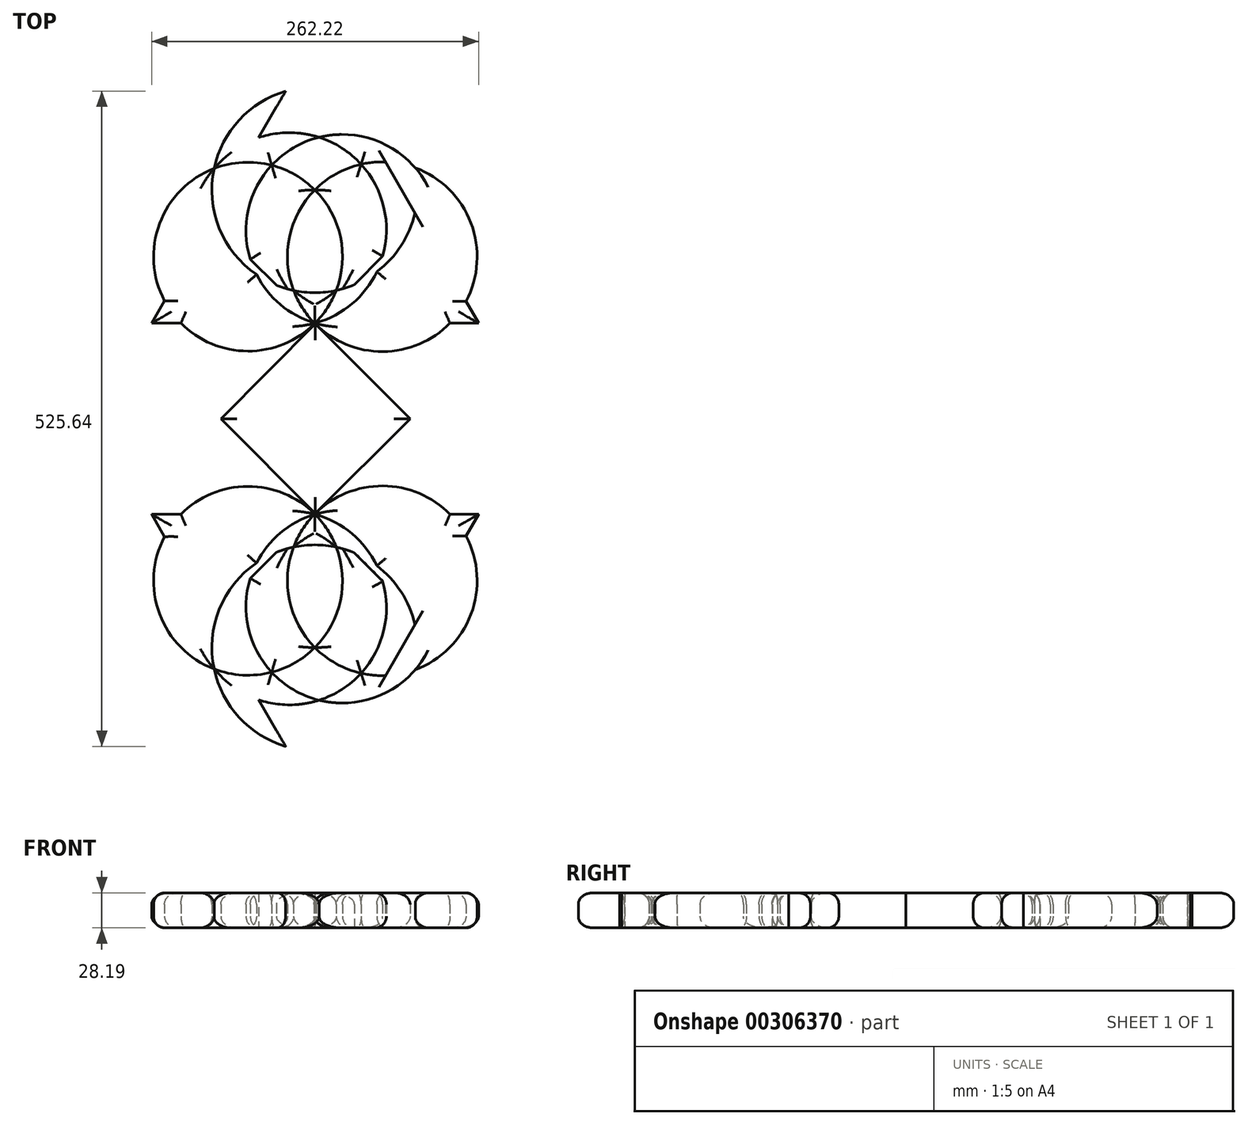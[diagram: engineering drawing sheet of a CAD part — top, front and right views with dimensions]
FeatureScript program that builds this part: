
annotation { "Feature Type Name" : "Feature", "Feature Type Description" : "" }
export const myFeature = defineFeature(function(context is Context, id is Id, definition is map)
    precondition{}
    {
        {
            var Q0;
            Q0=qCreatedBy(makeId("Top.planeOp"),FACE);
            var sketch = newSketch(context, id + "F0", { "sketchPlane" : qUnion([Q0])});
            skLineSegment(sketch, "E0", {"start": v(76.23, -76.68) * mm, "end": v(-75.62, -76.68) * mm});
            skLineSegment(sketch, "E1", {"start": v(-75.62, -76.68) * mm, "end": v(75.93, 75.47) * mm});
            skCircle(sketch, "E2", {"center": v(-53.8, 53.35) * mm, "radius": 75.78 * mm});
            skCircle(sketch, "E3", {"center": v(53.85, 53.3) * mm, "radius": 76.1 * mm});
            skCircle(sketch, "E4", {"center": v(-0.3, 107.01) * mm, "radius": 82.5 * mm});
            skLineSegment(sketch, "E5", {"start": v(76.23, -76.68) * mm, "end": v(-76.75, 76) * mm});
            skArc(sketch, "E6", {"start": v(0, 0) * mm, "mid": v(44.55, 117.58) * mm, "end": v(-81.01, 124.08) * mm});
            skArc(sketch, "E7", {"start": v(80.28, 124.67) * mm, "mid": v(-43.14, 115.96) * mm, "end": v(0, 0) * mm});
            skCircle(sketch, "E8.cCircle", {"center": v(0, 75.7) * mm, "radius": 75.7 * mm, "construction": true});
            skLineSegment(sketch, "E8.0", {"start": v(131.11, 0) * mm, "end": v(-131.11, 0) * mm});
            skLineSegment(sketch, "E8.1", {"start": v(-131.11, 0) * mm, "end": v(0, 227.1) * mm});
            skLineSegment(sketch, "E8.2", {"start": v(0, 227.1) * mm, "end": v(131.11, 0) * mm});
            skPoint(sketch, "E8.0.midPoint", {"position": v(0, 0) * mm});
            skSolve(sketch);
        }
        {
            var Q0;
            {var subQ0=sQuery(id+"F0.wireOp",EDGE,"E8.1");var subQ1=sQuery(id+"F0.wireOp",EDGE,"E2");var subQ2=makeQuery(id+"F0.imprint","INTERSECT",VERTEX,{"disambiguationData":[OD(0.0)],"derivedFrom":[subQ1,subQ0]});Q0=makeQuery(id+"F0.imprint","IMPRINT",FACE,{"disambiguationData":[TD([[makeQuery(id+"F0.imprint","IMPRINT",EDGE,{"disambiguationData":[TD([[subQ2,-1.0]])],"derivedFrom":subQ1}),-1.0]])]});}
            var Q1;
            {var subQ8=sQuery(id+"F0.wireOp",EDGE,"E8.1");var subQ9=sQuery(id+"F0.wireOp",EDGE,"E2");var subQ10=makeQuery(id+"F0.imprint","INTERSECT",VERTEX,{"disambiguationData":[OD(0.0)],"derivedFrom":[subQ9,subQ8]});Q1=makeQuery(id+"F0.imprint","IMPRINT",FACE,{"disambiguationData":[TD([[makeQuery(id+"F0.imprint","IMPRINT",EDGE,{"disambiguationData":[TD([[subQ10,-1.0]])],"derivedFrom":subQ9}),1.0]])]});}
            var Q2;
            {var subQ1=sQuery(id+"F0.wireOp",EDGE,"E4");var subQ7=sQuery(id+"F0.wireOp",EDGE,"E8.2");var subQ9=makeQuery(id+"F0.imprint","INTERSECT",VERTEX,{"disambiguationData":[OD(0.0)],"derivedFrom":[subQ1,subQ7]});Q2=makeQuery(id+"F0.imprint","IMPRINT",FACE,{"disambiguationData":[TD([[makeQuery(id+"F0.imprint","IMPRINT",EDGE,{"disambiguationData":[TD([[subQ9,-1.0]])],"derivedFrom":subQ1}),1.0]])]});}
            var Q3;
            {var subQ0=sQuery(id+"F0.wireOp",EDGE,"E8.0");var subQ1=sQuery(id+"F0.wireOp",EDGE,"E3");var subQ2=makeQuery(id+"F0.imprint","INTERSECT",VERTEX,{"disambiguationData":[OD(0.0)],"derivedFrom":[subQ1,subQ0]});Q3=makeQuery(id+"F0.imprint","IMPRINT",FACE,{"disambiguationData":[TD([[makeQuery(id+"F0.imprint","IMPRINT",EDGE,{"disambiguationData":[TD([[subQ2,-1.0]])],"derivedFrom":subQ1}),-1.0]])]});}
            var Q4;
            {var subQ1=sQuery(id+"F0.wireOp",EDGE,"E1");var subQ8=sQuery(id+"F0.wireOp",EDGE,"E8.0");var subQ12=makeQuery(id+"F0.imprint","INTERSECT",VERTEX,{"derivedFrom":[subQ1,subQ8]});Q4=makeQuery(id+"F0.imprint","IMPRINT",FACE,{"disambiguationData":[TD([[makeQuery(id+"F0.imprint","IMPRINT",EDGE,{"disambiguationData":[TD([[subQ12,-1.0]])],"derivedFrom":subQ1}),-1.0]])]});}
            var Q5;
            {var subQ0=sQuery(id+"F0.wireOp",EDGE,"E8.2");var subQ1=sQuery(id+"F0.wireOp",EDGE,"E4");var subQ2=makeQuery(id+"F0.imprint","INTERSECT",VERTEX,{"disambiguationData":[OD(0.0)],"derivedFrom":[subQ1,subQ0]});Q5=makeQuery(id+"F0.imprint","IMPRINT",FACE,{"disambiguationData":[TD([[makeQuery(id+"F0.imprint","IMPRINT",EDGE,{"disambiguationData":[TD([[subQ2,-1.0]])],"derivedFrom":subQ1}),-1.0]])]});}
            var Q6;
            {var subQ0=sQuery(id+"F0.wireOp",EDGE,"E0");Q6=makeQuery(id+"F0.imprint","IMPRINT",FACE,{"disambiguationData":[TD([[makeQuery(id+"F0.imprint","IMPRINT",EDGE,{"derivedFrom":subQ0}),-1.0]])]});}
            var Q7;
            {var subQ5=sQuery(id+"F0.wireOp",EDGE,"E2");var subQ7=sQuery(id+"F0.wireOp",EDGE,"E7");var subQ9=makeQuery(id+"F0.imprint","INTERSECT",VERTEX,{"derivedFrom":[subQ5,subQ7]});Q7=makeQuery(id+"F0.imprint","IMPRINT",FACE,{"disambiguationData":[TD([[makeQuery(id+"F0.imprint","IMPRINT",EDGE,{"disambiguationData":[TD([[subQ9,1.0]])],"derivedFrom":subQ5}),1.0]])]});}
            var Q8;
            {var subQ0=sQuery(id+"F0.wireOp",EDGE,"E4");var subQ1=sQuery(id+"F0.wireOp",EDGE,"E1");var subQ2=makeQuery(id+"F0.imprint","INTERSECT",VERTEX,{"disambiguationData":[OD(1.0)],"derivedFrom":[subQ1,subQ0]});Q8=makeQuery(id+"F0.imprint","IMPRINT",FACE,{"disambiguationData":[TD([[makeQuery(id+"F0.imprint","IMPRINT",EDGE,{"disambiguationData":[TD([[subQ2,-1.0]])],"derivedFrom":subQ1}),1.0]])]});}
            var Q9;
            {var subQ0=sQuery(id+"F0.wireOp",EDGE,"E8.2");var subQ1=sQuery(id+"F0.wireOp",EDGE,"E3");var subQ2=makeQuery(id+"F0.imprint","INTERSECT",VERTEX,{"disambiguationData":[OD(1.0)],"derivedFrom":[subQ1,subQ0]});Q9=makeQuery(id+"F0.imprint","IMPRINT",FACE,{"disambiguationData":[TD([[makeQuery(id+"F0.imprint","IMPRINT",EDGE,{"disambiguationData":[TD([[subQ2,-1.0]])],"derivedFrom":subQ1}),-1.0]])]});}
            var Q10;
            {var subQ0=sQuery(id+"F0.wireOp",EDGE,"E7");var subQ1=sQuery(id+"F0.wireOp",EDGE,"E2");var subQ2=makeQuery(id+"F0.imprint","INTERSECT",VERTEX,{"derivedFrom":[subQ1,subQ0]});Q10=makeQuery(id+"F0.imprint","IMPRINT",FACE,{"disambiguationData":[TD([[makeQuery(id+"F0.imprint","IMPRINT",EDGE,{"disambiguationData":[TD([[subQ2,-1.0]])],"derivedFrom":subQ1}),-1.0]])]});}
            var Q11;
            {var subQ3=sQuery(id+"F0.wireOp",EDGE,"E4");var subQ5=sQuery(id+"F0.wireOp",EDGE,"E3");var subQ6=makeQuery(id+"F0.imprint","INTERSECT",VERTEX,{"derivedFrom":[subQ5,subQ3]});Q11=makeQuery(id+"F0.imprint","IMPRINT",FACE,{"disambiguationData":[TD([[makeQuery(id+"F0.imprint","IMPRINT",EDGE,{"disambiguationData":[TD([[subQ6,-1.0]])],"derivedFrom":subQ5}),1.0]])]});}
            var Q12;
            {var subQ1=sQuery(id+"F0.wireOp",EDGE,"E2");var subQ3=sQuery(id+"F0.wireOp",EDGE,"E8.1");var subQ4=makeQuery(id+"F0.imprint","INTERSECT",VERTEX,{"disambiguationData":[OD(0.0)],"derivedFrom":[subQ1,subQ3]});Q12=makeQuery(id+"F0.imprint","IMPRINT",FACE,{"disambiguationData":[TD([[makeQuery(id+"F0.imprint","IMPRINT",EDGE,{"disambiguationData":[TD([[subQ4,-1.0]])],"derivedFrom":subQ3}),1.0]])]});}
            var Q13;
            {var subQ0=sQuery(id+"F0.wireOp",EDGE,"E8.0");var subQ1=sQuery(id+"F0.wireOp",EDGE,"E2");var subQ2=makeQuery(id+"F0.imprint","INTERSECT",VERTEX,{"derivedFrom":[subQ1,subQ0]});Q13=makeQuery(id+"F0.imprint","IMPRINT",FACE,{"disambiguationData":[TD([[makeQuery(id+"F0.imprint","IMPRINT",EDGE,{"disambiguationData":[TD([[subQ2,-1.0]])],"derivedFrom":subQ1}),1.0]])]});}
            var Q14;
            {var subQ0=sQuery(id+"F0.wireOp",EDGE,"E3");var subQ1=sQuery(id+"F0.wireOp",EDGE,"E1");var subQ2=makeQuery(id+"F0.imprint","INTERSECT",VERTEX,{"derivedFrom":[subQ1,subQ0]});Q14=makeQuery(id+"F0.imprint","IMPRINT",FACE,{"disambiguationData":[TD([[makeQuery(id+"F0.imprint","IMPRINT",EDGE,{"disambiguationData":[TD([[subQ2,-1.0]])],"derivedFrom":subQ1}),-1.0]])]});}
            var Q15;
            {var subQ1=sQuery(id+"F0.wireOp",EDGE,"E3");var subQ3=sQuery(id+"F0.wireOp",EDGE,"E8.2");var subQ4=makeQuery(id+"F0.imprint","INTERSECT",VERTEX,{"disambiguationData":[OD(0.0)],"derivedFrom":[subQ1,subQ3]});Q15=makeQuery(id+"F0.imprint","IMPRINT",FACE,{"disambiguationData":[TD([[makeQuery(id+"F0.imprint","IMPRINT",EDGE,{"disambiguationData":[TD([[subQ4,1.0]])],"derivedFrom":subQ3}),1.0]])]});}
            var Q16;
            {var subQ1=sQuery(id+"F0.wireOp",EDGE,"E4");var subQ3=sQuery(id+"F0.wireOp",EDGE,"E8.2");var subQ4=makeQuery(id+"F0.imprint","INTERSECT",VERTEX,{"disambiguationData":[OD(0.0)],"derivedFrom":[subQ1,subQ3]});Q16=makeQuery(id+"F0.imprint","IMPRINT",FACE,{"disambiguationData":[TD([[makeQuery(id+"F0.imprint","IMPRINT",EDGE,{"disambiguationData":[TD([[subQ4,-1.0]])],"derivedFrom":subQ3}),1.0]])]});}
            var Q17;
            {var subQ1=sQuery(id+"F0.wireOp",EDGE,"E4");var subQ3=sQuery(id+"F0.wireOp",EDGE,"E8.1");var subQ4=makeQuery(id+"F0.imprint","INTERSECT",VERTEX,{"disambiguationData":[OD(0.0)],"derivedFrom":[subQ1,subQ3]});Q17=makeQuery(id+"F0.imprint","IMPRINT",FACE,{"disambiguationData":[TD([[makeQuery(id+"F0.imprint","IMPRINT",EDGE,{"disambiguationData":[TD([[subQ4,1.0]])],"derivedFrom":subQ3}),1.0]])]});}
            var Q18;
            {var subQ1=sQuery(id+"F0.wireOp",EDGE,"E2");var subQ3=sQuery(id+"F0.wireOp",EDGE,"E8.1");var subQ4=makeQuery(id+"F0.imprint","INTERSECT",VERTEX,{"disambiguationData":[OD(1.0)],"derivedFrom":[subQ1,subQ3]});Q18=makeQuery(id+"F0.imprint","IMPRINT",FACE,{"disambiguationData":[TD([[makeQuery(id+"F0.imprint","IMPRINT",EDGE,{"disambiguationData":[TD([[subQ4,-1.0]])],"derivedFrom":subQ3}),1.0]])]});}
            var Q19;
            {var subQ1=sQuery(id+"F0.wireOp",EDGE,"E3");var subQ3=sQuery(id+"F0.wireOp",EDGE,"E8.2");var subQ4=makeQuery(id+"F0.imprint","INTERSECT",VERTEX,{"disambiguationData":[OD(1.0)],"derivedFrom":[subQ1,subQ3]});Q19=makeQuery(id+"F0.imprint","IMPRINT",FACE,{"disambiguationData":[TD([[makeQuery(id+"F0.imprint","IMPRINT",EDGE,{"disambiguationData":[TD([[subQ4,1.0]])],"derivedFrom":subQ3}),1.0]])]});}
            extrude(context, id + "F1", {"entities" : qUnion([Q0, Q1, Q2, Q3, Q4, Q5, Q6, Q7, Q8, Q9, Q10, Q11, Q12, Q13, Q14, Q15, Q16, Q17, Q18, Q19]), "depth" : 28.2 * mm});
        }
        {
            var Q0;
            {var subQ0=sQuery(id+"F0.wireOp",EDGE,"E2");Q0=makeQuery(id+"F1.opExtrude","CAP_EDGE",EDGE,{"disambiguationData":[OSD([subQ0]),TDD([makeQuery(id+"F0.imprint","IMPRINT",EDGE,{"disambiguationData":[TD([[makeQuery(id+"F0.imprint","INTERSECT",VERTEX,{"disambiguationData":[OD(0.0)],"derivedFrom":[subQ0,sQuery(id+"F0.wireOp",EDGE,"E8.1")]}),1.0]])],"derivedFrom":subQ0})])],"isStart":true});}
            var Q1;
            {var subQ0=sQuery(id+"F0.wireOp",EDGE,"E8.1");Q1=makeQuery(id+"F1.opExtrude","CAP_EDGE",EDGE,{"disambiguationData":[OSD([subQ0]),TDD([makeQuery(id+"F0.imprint","IMPRINT",EDGE,{"disambiguationData":[TD([[makeQuery(id+"F0.imprint","INTERSECT",VERTEX,{"derivedFrom":[sQuery(id+"F0.wireOp",EDGE,"E8.0"),subQ0]}),-1.0]])],"derivedFrom":subQ0})])],"isStart":true});}
            var Q2;
            {var subQ0=sQuery(id+"F0.wireOp",EDGE,"E2");Q2=makeQuery(id+"F1.opExtrude","CAP_EDGE",EDGE,{"disambiguationData":[OSD([subQ0]),TDD([makeQuery(id+"F0.imprint","IMPRINT",EDGE,{"disambiguationData":[TD([[makeQuery(id+"F0.imprint","INTERSECT",VERTEX,{"derivedFrom":[subQ0,sQuery(id+"F0.wireOp",EDGE,"E8.0")]}),-1.0]])],"derivedFrom":subQ0})])],"isStart":true});}
            var Q3;
            {var subQ0=sQuery(id+"F0.wireOp",EDGE,"E8.0");Q3=makeQuery(id+"F1.opExtrude","CAP_EDGE",EDGE,{"disambiguationData":[OSD([subQ0]),TDD([makeQuery(id+"F0.imprint","IMPRINT",EDGE,{"disambiguationData":[TD([[makeQuery(id+"F0.imprint","INTERSECT",VERTEX,{"derivedFrom":[subQ0,sQuery(id+"F0.wireOp",EDGE,"E8.1")]}),1.0]])],"derivedFrom":subQ0})])],"isStart":true});}
            var Q4;
            {var subQ0=sQuery(id+"F0.wireOp",EDGE,"E2");Q4=makeQuery(id+"F1.opExtrude","CAP_EDGE",EDGE,{"disambiguationData":[OSD([subQ0]),TDD([makeQuery(id+"F0.imprint","IMPRINT",EDGE,{"disambiguationData":[TD([[makeQuery(id+"F0.imprint","INTERSECT",VERTEX,{"derivedFrom":[subQ0,sQuery(id+"F0.wireOp",EDGE,"E8.0")]}),-1.0]])],"derivedFrom":subQ0})])],"isStart":false});}
            var Q5;
            {var subQ0=sQuery(id+"F0.wireOp",EDGE,"E8.0");Q5=makeQuery(id+"F1.opExtrude","CAP_EDGE",EDGE,{"disambiguationData":[OSD([subQ0]),TDD([makeQuery(id+"F0.imprint","IMPRINT",EDGE,{"disambiguationData":[TD([[makeQuery(id+"F0.imprint","INTERSECT",VERTEX,{"derivedFrom":[subQ0,sQuery(id+"F0.wireOp",EDGE,"E8.1")]}),1.0]])],"derivedFrom":subQ0})])],"isStart":false});}
            var Q6;
            {var subQ0=sQuery(id+"F0.wireOp",EDGE,"E2");Q6=makeQuery(id+"F1.opExtrude","CAP_EDGE",EDGE,{"disambiguationData":[OSD([subQ0]),TDD([makeQuery(id+"F0.imprint","IMPRINT",EDGE,{"disambiguationData":[TD([[makeQuery(id+"F0.imprint","INTERSECT",VERTEX,{"disambiguationData":[OD(0.0)],"derivedFrom":[subQ0,sQuery(id+"F0.wireOp",EDGE,"E8.1")]}),1.0]])],"derivedFrom":subQ0})])],"isStart":false});}
            var Q7;
            {var subQ0=sQuery(id+"F0.wireOp",EDGE,"E8.1");Q7=makeQuery(id+"F1.opExtrude","CAP_EDGE",EDGE,{"disambiguationData":[OSD([subQ0]),TDD([makeQuery(id+"F0.imprint","IMPRINT",EDGE,{"disambiguationData":[TD([[makeQuery(id+"F0.imprint","INTERSECT",VERTEX,{"derivedFrom":[sQuery(id+"F0.wireOp",EDGE,"E8.0"),subQ0]}),-1.0]])],"derivedFrom":subQ0})])],"isStart":false});}
            var Q8;
            {var subQ0=sQuery(id+"F0.wireOp",EDGE,"E4");var subQ1=makeQuery(id+"F0.imprint","INTERSECT",VERTEX,{"disambiguationData":[OD(0.0)],"derivedFrom":[subQ0,sQuery(id+"F0.wireOp",EDGE,"E5")]});var subQ2=makeQuery(id+"F0.imprint","INTERSECT",VERTEX,{"disambiguationData":[OD(1.0)],"derivedFrom":[subQ0,sQuery(id+"F0.wireOp",EDGE,"E8.1")]});Q8=makeQuery(id+"F1.opExtrude","CAP_EDGE",EDGE,{"disambiguationData":[OSD([subQ0]),TDD([makeQuery(id+"F0.imprint","IMPRINT",EDGE,{"disambiguationData":[TD([[subQ2,1.0]])],"derivedFrom":subQ0}),makeQuery(id+"F0.imprint","IMPRINT",EDGE,{"disambiguationData":[TD([[subQ1,1.0]])],"derivedFrom":subQ0}),makeQuery(id+"F0.imprint","IMPRINT",EDGE,{"disambiguationData":[TD([[subQ1,-1.0]])],"derivedFrom":subQ0})])],"isStart":true});}
            var Q9;
            {var subQ0=sQuery(id+"F0.wireOp",EDGE,"E4");Q9=makeQuery(id+"F1.opExtrude","CAP_EDGE",EDGE,{"disambiguationData":[OSD([subQ0]),TDD([makeQuery(id+"F0.imprint","IMPRINT",EDGE,{"disambiguationData":[TD([[makeQuery(id+"F0.imprint","INTERSECT",VERTEX,{"derivedFrom":[sQuery(id+"F0.wireOp",EDGE,"E3"),subQ0]}),1.0]])],"derivedFrom":subQ0})])],"isStart":true});}
            var Q10;
            {var subQ0=sQuery(id+"F0.wireOp",EDGE,"E7");Q10=makeQuery(id+"F1.opExtrude","CAP_EDGE",EDGE,{"disambiguationData":[OSD([subQ0]),TDD([makeQuery(id+"F0.imprint","IMPRINT",EDGE,{"disambiguationData":[TD([[makeQuery(id+"F0.imprint","INTERSECT",VERTEX,{"derivedFrom":[sQuery(id+"F0.wireOp",EDGE,"E4"),subQ0]}),-1.0]])],"derivedFrom":subQ0})])],"isStart":false});}
            var Q11;
            {var subQ0=sQuery(id+"F0.wireOp",EDGE,"E7");Q11=makeQuery(id+"F1.opExtrude","CAP_EDGE",EDGE,{"disambiguationData":[OSD([subQ0]),TDD([makeQuery(id+"F0.imprint","IMPRINT",EDGE,{"disambiguationData":[TD([[makeQuery(id+"F0.imprint","INTERSECT",VERTEX,{"derivedFrom":[sQuery(id+"F0.wireOp",EDGE,"E4"),subQ0]}),-1.0]])],"derivedFrom":subQ0})])],"isStart":true});}
            var Q12;
            {var subQ0=sQuery(id+"F0.wireOp",EDGE,"E4");var subQ1=makeQuery(id+"F0.imprint","INTERSECT",VERTEX,{"disambiguationData":[OD(0.0)],"derivedFrom":[subQ0,sQuery(id+"F0.wireOp",EDGE,"E5")]});var subQ2=makeQuery(id+"F0.imprint","INTERSECT",VERTEX,{"disambiguationData":[OD(1.0)],"derivedFrom":[subQ0,sQuery(id+"F0.wireOp",EDGE,"E8.1")]});Q12=makeQuery(id+"F1.opExtrude","CAP_EDGE",EDGE,{"disambiguationData":[OSD([subQ0]),TDD([makeQuery(id+"F0.imprint","IMPRINT",EDGE,{"disambiguationData":[TD([[subQ2,1.0]])],"derivedFrom":subQ0}),makeQuery(id+"F0.imprint","IMPRINT",EDGE,{"disambiguationData":[TD([[subQ1,1.0]])],"derivedFrom":subQ0}),makeQuery(id+"F0.imprint","IMPRINT",EDGE,{"disambiguationData":[TD([[subQ1,-1.0]])],"derivedFrom":subQ0})])],"isStart":false});}
            var Q13;
            {var subQ0=sQuery(id+"F0.wireOp",EDGE,"E5");Q13=makeQuery(id+"F1.opExtrude","CAP_EDGE",EDGE,{"disambiguationData":[OSD([subQ0]),TDD([makeQuery(id+"F0.imprint","IMPRINT",EDGE,{"disambiguationData":[TD([[makeQuery(id+"F0.imprint","INTERSECT",VERTEX,{"disambiguationData":[OD(1.0)],"derivedFrom":[sQuery(id+"F0.wireOp",EDGE,"E4"),subQ0]}),-1.0]])],"derivedFrom":subQ0})])],"isStart":false});}
            var Q14;
            {var subQ0=sQuery(id+"F0.wireOp",EDGE,"E4");Q14=makeQuery(id+"F1.opExtrude","CAP_EDGE",EDGE,{"disambiguationData":[OSD([subQ0]),TDD([makeQuery(id+"F0.imprint","IMPRINT",EDGE,{"disambiguationData":[TD([[makeQuery(id+"F0.imprint","INTERSECT",VERTEX,{"derivedFrom":[sQuery(id+"F0.wireOp",EDGE,"E3"),subQ0]}),1.0]])],"derivedFrom":subQ0})])],"isStart":false});}
            var Q15;
            {var subQ0=sQuery(id+"F0.wireOp",EDGE,"E5");Q15=makeQuery(id+"F1.opExtrude","CAP_EDGE",EDGE,{"disambiguationData":[OSD([subQ0]),TDD([makeQuery(id+"F0.imprint","IMPRINT",EDGE,{"disambiguationData":[TD([[makeQuery(id+"F0.imprint","INTERSECT",VERTEX,{"disambiguationData":[OD(1.0)],"derivedFrom":[sQuery(id+"F0.wireOp",EDGE,"E4"),subQ0]}),-1.0]])],"derivedFrom":subQ0})])],"isStart":true});}
            var Q16;
            {var subQ0=sQuery(id+"F0.wireOp",EDGE,"E7");Q16=makeQuery(id+"F1.opExtrude","CAP_EDGE",EDGE,{"disambiguationData":[OSD([subQ0]),TDD([makeQuery(id+"F0.imprint","IMPRINT",EDGE,{"disambiguationData":[TD([[makeQuery(id+"F0.imprint","INTERSECT",VERTEX,{"derivedFrom":[sQuery(id+"F0.wireOp",EDGE,"E2"),subQ0]}),-1.0]])],"derivedFrom":subQ0})])],"isStart":false});}
            var Q17;
            {var subQ0=sQuery(id+"F0.wireOp",EDGE,"E7");Q17=makeQuery(id+"F1.opExtrude","CAP_EDGE",EDGE,{"disambiguationData":[OSD([subQ0]),TDD([makeQuery(id+"F0.imprint","IMPRINT",EDGE,{"disambiguationData":[TD([[makeQuery(id+"F0.imprint","INTERSECT",VERTEX,{"derivedFrom":[sQuery(id+"F0.wireOp",EDGE,"E2"),subQ0]}),-1.0]])],"derivedFrom":subQ0})])],"isStart":true});}
            var Q18;
            {var subQ0=sQuery(id+"F0.wireOp",EDGE,"E2");Q18=makeQuery(id+"F1.opExtrude","CAP_EDGE",EDGE,{"disambiguationData":[OSD([subQ0]),TDD([makeQuery(id+"F0.imprint","IMPRINT",EDGE,{"disambiguationData":[TD([[makeQuery(id+"F0.imprint","INTERSECT",VERTEX,{"derivedFrom":[subQ0,sQuery(id+"F0.wireOp",EDGE,"E7")]}),1.0]])],"derivedFrom":subQ0})])],"isStart":false});}
            var Q19;
            {var subQ0=sQuery(id+"F0.wireOp",EDGE,"E3");Q19=makeQuery(id+"F1.opExtrude","CAP_EDGE",EDGE,{"disambiguationData":[OSD([subQ0]),TDD([makeQuery(id+"F0.imprint","IMPRINT",EDGE,{"disambiguationData":[TD([[makeQuery(id+"F0.imprint","INTERSECT",VERTEX,{"disambiguationData":[OD(0.0)],"derivedFrom":[sQuery(id+"F0.wireOp",EDGE,"E2"),subQ0]}),-1.0]])],"derivedFrom":subQ0})])],"isStart":false});}
            var Q20;
            {var subQ0=sQuery(id+"F0.wireOp",EDGE,"E2");Q20=makeQuery(id+"F1.opExtrude","CAP_EDGE",EDGE,{"disambiguationData":[OSD([subQ0]),TDD([makeQuery(id+"F0.imprint","IMPRINT",EDGE,{"disambiguationData":[TD([[makeQuery(id+"F0.imprint","INTERSECT",VERTEX,{"disambiguationData":[OD(0.0)],"derivedFrom":[subQ0,sQuery(id+"F0.wireOp",EDGE,"E3")]}),1.0]])],"derivedFrom":subQ0})])],"isStart":false});}
            var Q21;
            {var subQ0=sQuery(id+"F0.wireOp",EDGE,"E2");Q21=makeQuery(id+"F1.opExtrude","CAP_EDGE",EDGE,{"disambiguationData":[OSD([subQ0]),TDD([makeQuery(id+"F0.imprint","IMPRINT",EDGE,{"disambiguationData":[TD([[makeQuery(id+"F0.imprint","INTERSECT",VERTEX,{"disambiguationData":[OD(0.0)],"derivedFrom":[subQ0,sQuery(id+"F0.wireOp",EDGE,"E3")]}),1.0]])],"derivedFrom":subQ0})])],"isStart":true});}
            var Q22;
            {var subQ0=sQuery(id+"F0.wireOp",EDGE,"E3");Q22=makeQuery(id+"F1.opExtrude","CAP_EDGE",EDGE,{"disambiguationData":[OSD([subQ0]),TDD([makeQuery(id+"F0.imprint","IMPRINT",EDGE,{"disambiguationData":[TD([[makeQuery(id+"F0.imprint","INTERSECT",VERTEX,{"disambiguationData":[OD(0.0)],"derivedFrom":[sQuery(id+"F0.wireOp",EDGE,"E2"),subQ0]}),1.0]])],"derivedFrom":subQ0})])],"isStart":false});}
            var Q23;
            {var subQ0=sQuery(id+"F0.wireOp",EDGE,"E3");Q23=makeQuery(id+"F1.opExtrude","CAP_EDGE",EDGE,{"disambiguationData":[OSD([subQ0]),TDD([makeQuery(id+"F0.imprint","IMPRINT",EDGE,{"disambiguationData":[TD([[makeQuery(id+"F0.imprint","INTERSECT",VERTEX,{"disambiguationData":[OD(0.0)],"derivedFrom":[sQuery(id+"F0.wireOp",EDGE,"E2"),subQ0]}),1.0]])],"derivedFrom":subQ0})])],"isStart":true});}
            var Q24;
            {var subQ0=sQuery(id+"F0.wireOp",EDGE,"E6");Q24=makeQuery(id+"F1.opExtrude","CAP_EDGE",EDGE,{"disambiguationData":[OSD([subQ0]),TDD([makeQuery(id+"F0.imprint","IMPRINT",EDGE,{"disambiguationData":[TD([[makeQuery(id+"F0.imprint","INTERSECT",VERTEX,{"disambiguationData":[OD(1.0)],"derivedFrom":[sQuery(id+"F0.wireOp",EDGE,"E1"),subQ0]}),-1.0]])],"derivedFrom":subQ0})])],"isStart":false});}
            var Q25;
            {var subQ0=sQuery(id+"F0.wireOp",EDGE,"E1");Q25=makeQuery(id+"F1.opExtrude","CAP_EDGE",EDGE,{"disambiguationData":[OSD([subQ0]),TDD([makeQuery(id+"F0.imprint","IMPRINT",EDGE,{"disambiguationData":[TD([[makeQuery(id+"F0.imprint","INTERSECT",VERTEX,{"disambiguationData":[OD(1.0)],"derivedFrom":[subQ0,sQuery(id+"F0.wireOp",EDGE,"E4")]}),-1.0]])],"derivedFrom":subQ0})])],"isStart":false});}
            var Q26;
            {var subQ0=sQuery(id+"F0.wireOp",EDGE,"E3");Q26=makeQuery(id+"F1.opExtrude","CAP_EDGE",EDGE,{"disambiguationData":[OSD([subQ0]),TDD([makeQuery(id+"F0.imprint","IMPRINT",EDGE,{"disambiguationData":[TD([[makeQuery(id+"F0.imprint","INTERSECT",VERTEX,{"derivedFrom":[sQuery(id+"F0.wireOp",EDGE,"E1"),subQ0]}),-1.0]])],"derivedFrom":subQ0})])],"isStart":false});}
            var Q27;
            {var subQ0=sQuery(id+"F0.wireOp",EDGE,"E8.0");Q27=makeQuery(id+"F1.opExtrude","CAP_EDGE",EDGE,{"disambiguationData":[OSD([subQ0]),TDD([makeQuery(id+"F0.imprint","IMPRINT",EDGE,{"disambiguationData":[TD([[makeQuery(id+"F0.imprint","INTERSECT",VERTEX,{"derivedFrom":[subQ0,sQuery(id+"F0.wireOp",EDGE,"E8.2")]}),-1.0]])],"derivedFrom":subQ0})])],"isStart":false});}
            var Q28;
            {var subQ0=sQuery(id+"F0.wireOp",EDGE,"E4");var subQ1=makeQuery(id+"F0.imprint","INTERSECT",VERTEX,{"disambiguationData":[OD(1.0)],"derivedFrom":[subQ0,sQuery(id+"F0.wireOp",EDGE,"E8.2")]});var subQ2=makeQuery(id+"F0.imprint","INTERSECT",VERTEX,{"disambiguationData":[OD(0.0)],"derivedFrom":[sQuery(id+"F0.wireOp",EDGE,"E1"),subQ0]});Q28=makeQuery(id+"F1.opExtrude","CAP_EDGE",EDGE,{"disambiguationData":[OSD([subQ0]),TDD([makeQuery(id+"F0.imprint","IMPRINT",EDGE,{"disambiguationData":[TD([[subQ2,1.0]])],"derivedFrom":subQ0}),makeQuery(id+"F0.imprint","IMPRINT",EDGE,{"disambiguationData":[TD([[subQ2,-1.0]])],"derivedFrom":subQ0}),makeQuery(id+"F0.imprint","IMPRINT",EDGE,{"disambiguationData":[TD([[subQ1,-1.0]])],"derivedFrom":subQ0})])],"isStart":false});}
            var Q29;
            {var subQ0=sQuery(id+"F0.wireOp",EDGE,"E6");Q29=makeQuery(id+"F1.opExtrude","CAP_EDGE",EDGE,{"disambiguationData":[OSD([subQ0]),TDD([makeQuery(id+"F0.imprint","IMPRINT",EDGE,{"disambiguationData":[TD([[makeQuery(id+"F0.imprint","INTERSECT",VERTEX,{"disambiguationData":[OD(0.0)],"derivedFrom":[sQuery(id+"F0.wireOp",EDGE,"E1"),subQ0]}),-1.0]])],"derivedFrom":subQ0})])],"isStart":false});}
            var Q30;
            {var subQ0=sQuery(id+"F0.wireOp",EDGE,"E4");Q30=makeQuery(id+"F1.opExtrude","CAP_EDGE",EDGE,{"disambiguationData":[OSD([subQ0]),TDD([makeQuery(id+"F0.imprint","IMPRINT",EDGE,{"disambiguationData":[TD([[makeQuery(id+"F0.imprint","INTERSECT",VERTEX,{"disambiguationData":[OD(1.0)],"derivedFrom":[sQuery(id+"F0.wireOp",EDGE,"E1"),subQ0]}),1.0]])],"derivedFrom":subQ0})])],"isStart":false});}
            var Q31;
            {var subQ0=sQuery(id+"F0.wireOp",EDGE,"E6");Q31=makeQuery(id+"F1.opExtrude","CAP_EDGE",EDGE,{"disambiguationData":[OSD([subQ0]),TDD([makeQuery(id+"F0.imprint","IMPRINT",EDGE,{"disambiguationData":[TD([[makeQuery(id+"F0.imprint","INTERSECT",VERTEX,{"disambiguationData":[OD(0.0)],"derivedFrom":[sQuery(id+"F0.wireOp",EDGE,"E1"),subQ0]}),-1.0]])],"derivedFrom":subQ0})])],"isStart":true});}
            var Q32;
            {var subQ0=sQuery(id+"F0.wireOp",EDGE,"E4");var subQ1=makeQuery(id+"F0.imprint","INTERSECT",VERTEX,{"disambiguationData":[OD(1.0)],"derivedFrom":[subQ0,sQuery(id+"F0.wireOp",EDGE,"E8.2")]});var subQ2=makeQuery(id+"F0.imprint","INTERSECT",VERTEX,{"disambiguationData":[OD(0.0)],"derivedFrom":[sQuery(id+"F0.wireOp",EDGE,"E1"),subQ0]});Q32=makeQuery(id+"F1.opExtrude","CAP_EDGE",EDGE,{"disambiguationData":[OSD([subQ0]),TDD([makeQuery(id+"F0.imprint","IMPRINT",EDGE,{"disambiguationData":[TD([[subQ2,1.0]])],"derivedFrom":subQ0}),makeQuery(id+"F0.imprint","IMPRINT",EDGE,{"disambiguationData":[TD([[subQ2,-1.0]])],"derivedFrom":subQ0}),makeQuery(id+"F0.imprint","IMPRINT",EDGE,{"disambiguationData":[TD([[subQ1,-1.0]])],"derivedFrom":subQ0})])],"isStart":true});}
            var Q33;
            {var subQ0=sQuery(id+"F0.wireOp",EDGE,"E6");Q33=makeQuery(id+"F1.opExtrude","CAP_EDGE",EDGE,{"disambiguationData":[OSD([subQ0]),TDD([makeQuery(id+"F0.imprint","IMPRINT",EDGE,{"disambiguationData":[TD([[makeQuery(id+"F0.imprint","INTERSECT",VERTEX,{"derivedFrom":[sQuery(id+"F0.wireOp",EDGE,"E3"),subQ0]}),-1.0]])],"derivedFrom":subQ0})])],"isStart":false});}
            var Q34;
            {var subQ0=sQuery(id+"F0.wireOp",EDGE,"E3");var subQ1=makeQuery(id+"F0.imprint","INTERSECT",VERTEX,{"disambiguationData":[OD(1.0)],"derivedFrom":[subQ0,sQuery(id+"F0.wireOp",EDGE,"E8.2")]});Q34=makeQuery(id+"F1.opExtrude","CAP_EDGE",EDGE,{"disambiguationData":[OSD([subQ0]),TDD([makeQuery(id+"F0.imprint","IMPRINT",EDGE,{"disambiguationData":[TD([[subQ1,1.0]])],"derivedFrom":subQ0}),makeQuery(id+"F0.imprint","IMPRINT",EDGE,{"disambiguationData":[TD([[subQ1,-1.0]])],"derivedFrom":subQ0})])],"isStart":false});}
            var Q35;
            {var subQ0=sQuery(id+"F0.wireOp",EDGE,"E7");Q35=makeQuery(id+"F1.opExtrude","CAP_EDGE",EDGE,{"disambiguationData":[OSD([subQ0]),TDD([makeQuery(id+"F0.imprint","IMPRINT",EDGE,{"disambiguationData":[TD([[makeQuery(id+"F0.imprint","INTERSECT",VERTEX,{"derivedFrom":[sQuery(id+"F0.wireOp",EDGE,"E2"),subQ0]}),1.0]])],"derivedFrom":subQ0})])],"isStart":false});}
            var Q36;
            {var subQ0=sQuery(id+"F0.wireOp",EDGE,"E4");Q36=makeQuery(id+"F1.opExtrude","CAP_EDGE",EDGE,{"disambiguationData":[OSD([subQ0]),TDD([makeQuery(id+"F0.imprint","IMPRINT",EDGE,{"disambiguationData":[TD([[makeQuery(id+"F0.imprint","INTERSECT",VERTEX,{"disambiguationData":[OD(0.0)],"derivedFrom":[subQ0,sQuery(id+"F0.wireOp",EDGE,"E8.1")]}),-1.0]])],"derivedFrom":subQ0})])],"isStart":false});}
            var Q37;
            {var subQ0=sQuery(id+"F0.wireOp",EDGE,"E4");Q37=makeQuery(id+"F1.opExtrude","CAP_EDGE",EDGE,{"disambiguationData":[OSD([subQ0]),TDD([makeQuery(id+"F0.imprint","IMPRINT",EDGE,{"disambiguationData":[TD([[makeQuery(id+"F0.imprint","INTERSECT",VERTEX,{"disambiguationData":[OD(0.0)],"derivedFrom":[subQ0,sQuery(id+"F0.wireOp",EDGE,"E8.1")]}),-1.0]])],"derivedFrom":subQ0})])],"isStart":true});}
            var Q38;
            {var subQ0=sQuery(id+"F0.wireOp",EDGE,"E2");var subQ1=makeQuery(id+"F0.imprint","INTERSECT",VERTEX,{"disambiguationData":[OD(1.0)],"derivedFrom":[subQ0,sQuery(id+"F0.wireOp",EDGE,"E8.1")]});Q38=makeQuery(id+"F1.opExtrude","CAP_EDGE",EDGE,{"disambiguationData":[OSD([subQ0]),TDD([makeQuery(id+"F0.imprint","IMPRINT",EDGE,{"disambiguationData":[TD([[makeQuery(id+"F0.imprint","INTERSECT",VERTEX,{"derivedFrom":[subQ0,sQuery(id+"F0.wireOp",EDGE,"E7")]}),-1.0]])],"derivedFrom":subQ0}),makeQuery(id+"F0.imprint","IMPRINT",EDGE,{"disambiguationData":[TD([[subQ1,-1.0]])],"derivedFrom":subQ0})])],"isStart":false});}
            var Q39;
            {var subQ0=sQuery(id+"F0.wireOp",EDGE,"E8.1");Q39=makeQuery(id+"F1.opExtrude","CAP_EDGE",EDGE,{"disambiguationData":[OSD([subQ0]),TDD([makeQuery(id+"F0.imprint","IMPRINT",EDGE,{"disambiguationData":[TD([[makeQuery(id+"F0.imprint","INTERSECT",VERTEX,{"derivedFrom":[subQ0,sQuery(id+"F0.wireOp",EDGE,"E8.2")]}),1.0]])],"derivedFrom":subQ0})])],"isStart":false});}
            var Q40;
            {var subQ0=sQuery(id+"F0.wireOp",EDGE,"E8.2");Q40=makeQuery(id+"F1.opExtrude","CAP_EDGE",EDGE,{"disambiguationData":[OSD([subQ0]),TDD([makeQuery(id+"F0.imprint","IMPRINT",EDGE,{"disambiguationData":[TD([[makeQuery(id+"F0.imprint","INTERSECT",VERTEX,{"derivedFrom":[sQuery(id+"F0.wireOp",EDGE,"E8.1"),subQ0]}),-1.0]])],"derivedFrom":subQ0})])],"isStart":false});}
            var Q41;
            {var subQ0=sQuery(id+"F0.wireOp",EDGE,"E4");Q41=makeQuery(id+"F1.opExtrude","CAP_EDGE",EDGE,{"disambiguationData":[OSD([subQ0]),TDD([makeQuery(id+"F0.imprint","IMPRINT",EDGE,{"disambiguationData":[TD([[makeQuery(id+"F0.imprint","INTERSECT",VERTEX,{"disambiguationData":[OD(0.0)],"derivedFrom":[subQ0,sQuery(id+"F0.wireOp",EDGE,"E8.2")]}),1.0]])],"derivedFrom":subQ0})])],"isStart":false});}
            var Q42;
            {var subQ0=sQuery(id+"F0.wireOp",EDGE,"E8.1");Q42=makeQuery(id+"F1.opExtrude","CAP_EDGE",EDGE,{"disambiguationData":[OSD([subQ0]),TDD([makeQuery(id+"F0.imprint","IMPRINT",EDGE,{"disambiguationData":[TD([[makeQuery(id+"F0.imprint","INTERSECT",VERTEX,{"derivedFrom":[subQ0,sQuery(id+"F0.wireOp",EDGE,"E8.2")]}),1.0]])],"derivedFrom":subQ0})])],"isStart":true});}
            var Q43;
            {var subQ0=sQuery(id+"F0.wireOp",EDGE,"E3");Q43=makeQuery(id+"F1.opExtrude","CAP_EDGE",EDGE,{"disambiguationData":[OSD([subQ0]),TDD([makeQuery(id+"F0.imprint","IMPRINT",EDGE,{"disambiguationData":[TD([[makeQuery(id+"F0.imprint","INTERSECT",VERTEX,{"disambiguationData":[OD(0.0)],"derivedFrom":[subQ0,sQuery(id+"F0.wireOp",EDGE,"E8.2")]}),-1.0]])],"derivedFrom":subQ0})])],"isStart":false});}
            var Q44;
            {var subQ0=sQuery(id+"F0.wireOp",EDGE,"E8.2");Q44=makeQuery(id+"F1.opExtrude","CAP_EDGE",EDGE,{"disambiguationData":[OSD([subQ0]),TDD([makeQuery(id+"F0.imprint","IMPRINT",EDGE,{"disambiguationData":[TD([[makeQuery(id+"F0.imprint","INTERSECT",VERTEX,{"derivedFrom":[sQuery(id+"F0.wireOp",EDGE,"E8.0"),subQ0]}),1.0]])],"derivedFrom":subQ0})])],"isStart":false});}
            var Q45;
            {var subQ0=sQuery(id+"F0.wireOp",EDGE,"E2");Q45=makeQuery(id+"F1.opExtrude","CAP_EDGE",EDGE,{"disambiguationData":[OSD([subQ0]),TDD([makeQuery(id+"F0.imprint","IMPRINT",EDGE,{"disambiguationData":[TD([[makeQuery(id+"F0.imprint","INTERSECT",VERTEX,{"derivedFrom":[subQ0,sQuery(id+"F0.wireOp",EDGE,"E4")]}),1.0]])],"derivedFrom":subQ0})])],"isStart":false});}
            var Q46;
            {var subQ0=sQuery(id+"F0.wireOp",EDGE,"E4");Q46=makeQuery(id+"F1.opExtrude","CAP_EDGE",EDGE,{"disambiguationData":[OSD([subQ0]),TDD([makeQuery(id+"F0.imprint","IMPRINT",EDGE,{"disambiguationData":[TD([[makeQuery(id+"F0.imprint","INTERSECT",VERTEX,{"derivedFrom":[sQuery(id+"F0.wireOp",EDGE,"E2"),subQ0]}),1.0]])],"derivedFrom":subQ0})])],"isStart":false});}
            var Q47;
            {var subQ0=sQuery(id+"F0.wireOp",EDGE,"E4");Q47=makeQuery(id+"F1.opExtrude","CAP_EDGE",EDGE,{"disambiguationData":[OSD([subQ0]),TDD([makeQuery(id+"F0.imprint","IMPRINT",EDGE,{"disambiguationData":[TD([[makeQuery(id+"F0.imprint","INTERSECT",VERTEX,{"derivedFrom":[sQuery(id+"F0.wireOp",EDGE,"E2"),subQ0]}),1.0]])],"derivedFrom":subQ0})])],"isStart":true});}
            var Q48;
            {var subQ0=sQuery(id+"F0.wireOp",EDGE,"E3");Q48=makeQuery(id+"F1.opExtrude","CAP_EDGE",EDGE,{"disambiguationData":[OSD([subQ0]),TDD([makeQuery(id+"F0.imprint","IMPRINT",EDGE,{"disambiguationData":[TD([[makeQuery(id+"F0.imprint","INTERSECT",VERTEX,{"derivedFrom":[subQ0,sQuery(id+"F0.wireOp",EDGE,"E4")]}),-1.0]])],"derivedFrom":subQ0})])],"isStart":false});}
            var Q49;
            {var subQ0=sQuery(id+"F0.wireOp",EDGE,"E3");Q49=makeQuery(id+"F1.opExtrude","CAP_EDGE",EDGE,{"disambiguationData":[OSD([subQ0]),TDD([makeQuery(id+"F0.imprint","IMPRINT",EDGE,{"disambiguationData":[TD([[makeQuery(id+"F0.imprint","INTERSECT",VERTEX,{"derivedFrom":[subQ0,sQuery(id+"F0.wireOp",EDGE,"E4")]}),-1.0]])],"derivedFrom":subQ0})])],"isStart":true});}
            var Q50;
            {var subQ0=sQuery(id+"F0.wireOp",EDGE,"E4");Q50=makeQuery(id+"F1.opExtrude","CAP_EDGE",EDGE,{"disambiguationData":[OSD([subQ0]),TDD([makeQuery(id+"F0.imprint","IMPRINT",EDGE,{"disambiguationData":[TD([[makeQuery(id+"F0.imprint","INTERSECT",VERTEX,{"disambiguationData":[OD(0.0)],"derivedFrom":[subQ0,sQuery(id+"F0.wireOp",EDGE,"E8.2")]}),1.0]])],"derivedFrom":subQ0})])],"isStart":true});}
            var Q51;
            {var subQ0=sQuery(id+"F0.wireOp",EDGE,"E8.2");Q51=makeQuery(id+"F1.opExtrude","CAP_EDGE",EDGE,{"disambiguationData":[OSD([subQ0]),TDD([makeQuery(id+"F0.imprint","IMPRINT",EDGE,{"disambiguationData":[TD([[makeQuery(id+"F0.imprint","INTERSECT",VERTEX,{"derivedFrom":[sQuery(id+"F0.wireOp",EDGE,"E8.1"),subQ0]}),-1.0]])],"derivedFrom":subQ0})])],"isStart":true});}
            var Q52;
            {var subQ0=sQuery(id+"F0.wireOp",EDGE,"E7");Q52=makeQuery(id+"F1.opExtrude","CAP_EDGE",EDGE,{"disambiguationData":[OSD([subQ0]),TDD([makeQuery(id+"F0.imprint","IMPRINT",EDGE,{"disambiguationData":[TD([[makeQuery(id+"F0.imprint","INTERSECT",VERTEX,{"derivedFrom":[sQuery(id+"F0.wireOp",EDGE,"E2"),subQ0]}),1.0]])],"derivedFrom":subQ0})])],"isStart":true});}
            var Q53;
            {var subQ0=sQuery(id+"F0.wireOp",EDGE,"E6");Q53=makeQuery(id+"F1.opExtrude","CAP_EDGE",EDGE,{"disambiguationData":[OSD([subQ0]),TDD([makeQuery(id+"F0.imprint","IMPRINT",EDGE,{"disambiguationData":[TD([[makeQuery(id+"F0.imprint","INTERSECT",VERTEX,{"derivedFrom":[sQuery(id+"F0.wireOp",EDGE,"E3"),subQ0]}),-1.0]])],"derivedFrom":subQ0})])],"isStart":true});}
            var Q54;
            {var subQ0=sQuery(id+"F0.wireOp",EDGE,"E3");var subQ1=makeQuery(id+"F0.imprint","INTERSECT",VERTEX,{"disambiguationData":[OD(1.0)],"derivedFrom":[subQ0,sQuery(id+"F0.wireOp",EDGE,"E8.2")]});Q54=makeQuery(id+"F1.opExtrude","CAP_EDGE",EDGE,{"disambiguationData":[OSD([subQ0]),TDD([makeQuery(id+"F0.imprint","IMPRINT",EDGE,{"disambiguationData":[TD([[subQ1,1.0]])],"derivedFrom":subQ0}),makeQuery(id+"F0.imprint","IMPRINT",EDGE,{"disambiguationData":[TD([[subQ1,-1.0]])],"derivedFrom":subQ0})])],"isStart":true});}
            var Q55;
            {var subQ0=sQuery(id+"F0.wireOp",EDGE,"E2");var subQ1=makeQuery(id+"F0.imprint","INTERSECT",VERTEX,{"disambiguationData":[OD(1.0)],"derivedFrom":[subQ0,sQuery(id+"F0.wireOp",EDGE,"E8.1")]});Q55=makeQuery(id+"F1.opExtrude","CAP_EDGE",EDGE,{"disambiguationData":[OSD([subQ0]),TDD([makeQuery(id+"F0.imprint","IMPRINT",EDGE,{"disambiguationData":[TD([[makeQuery(id+"F0.imprint","INTERSECT",VERTEX,{"derivedFrom":[subQ0,sQuery(id+"F0.wireOp",EDGE,"E7")]}),-1.0]])],"derivedFrom":subQ0}),makeQuery(id+"F0.imprint","IMPRINT",EDGE,{"disambiguationData":[TD([[subQ1,-1.0]])],"derivedFrom":subQ0})])],"isStart":true});}
            var Q56;
            {var subQ0=sQuery(id+"F0.wireOp",EDGE,"E2");Q56=makeQuery(id+"F1.opExtrude","CAP_EDGE",EDGE,{"disambiguationData":[OSD([subQ0]),TDD([makeQuery(id+"F0.imprint","IMPRINT",EDGE,{"disambiguationData":[TD([[makeQuery(id+"F0.imprint","INTERSECT",VERTEX,{"derivedFrom":[subQ0,sQuery(id+"F0.wireOp",EDGE,"E7")]}),1.0]])],"derivedFrom":subQ0})])],"isStart":true});}
            var Q57;
            {var subQ0=sQuery(id+"F0.wireOp",EDGE,"E3");Q57=makeQuery(id+"F1.opExtrude","CAP_EDGE",EDGE,{"disambiguationData":[OSD([subQ0]),TDD([makeQuery(id+"F0.imprint","IMPRINT",EDGE,{"disambiguationData":[TD([[makeQuery(id+"F0.imprint","INTERSECT",VERTEX,{"disambiguationData":[OD(0.0)],"derivedFrom":[sQuery(id+"F0.wireOp",EDGE,"E2"),subQ0]}),-1.0]])],"derivedFrom":subQ0})])],"isStart":true});}
            var Q58;
            {var subQ0=sQuery(id+"F0.wireOp",EDGE,"E6");Q58=makeQuery(id+"F1.opExtrude","CAP_EDGE",EDGE,{"disambiguationData":[OSD([subQ0]),TDD([makeQuery(id+"F0.imprint","IMPRINT",EDGE,{"disambiguationData":[TD([[makeQuery(id+"F0.imprint","INTERSECT",VERTEX,{"disambiguationData":[OD(1.0)],"derivedFrom":[sQuery(id+"F0.wireOp",EDGE,"E1"),subQ0]}),-1.0]])],"derivedFrom":subQ0})])],"isStart":true});}
            var Q59;
            {var subQ0=sQuery(id+"F0.wireOp",EDGE,"E3");Q59=makeQuery(id+"F1.opExtrude","CAP_EDGE",EDGE,{"disambiguationData":[OSD([subQ0]),TDD([makeQuery(id+"F0.imprint","IMPRINT",EDGE,{"disambiguationData":[TD([[makeQuery(id+"F0.imprint","INTERSECT",VERTEX,{"disambiguationData":[OD(0.0)],"derivedFrom":[subQ0,sQuery(id+"F0.wireOp",EDGE,"E8.2")]}),-1.0]])],"derivedFrom":subQ0})])],"isStart":true});}
            var Q60;
            {var subQ0=sQuery(id+"F0.wireOp",EDGE,"E8.2");Q60=makeQuery(id+"F1.opExtrude","CAP_EDGE",EDGE,{"disambiguationData":[OSD([subQ0]),TDD([makeQuery(id+"F0.imprint","IMPRINT",EDGE,{"disambiguationData":[TD([[makeQuery(id+"F0.imprint","INTERSECT",VERTEX,{"derivedFrom":[sQuery(id+"F0.wireOp",EDGE,"E8.0"),subQ0]}),1.0]])],"derivedFrom":subQ0})])],"isStart":true});}
            var Q61;
            {var subQ0=sQuery(id+"F0.wireOp",EDGE,"E8.0");Q61=makeQuery(id+"F1.opExtrude","CAP_EDGE",EDGE,{"disambiguationData":[OSD([subQ0]),TDD([makeQuery(id+"F0.imprint","IMPRINT",EDGE,{"disambiguationData":[TD([[makeQuery(id+"F0.imprint","INTERSECT",VERTEX,{"derivedFrom":[subQ0,sQuery(id+"F0.wireOp",EDGE,"E8.2")]}),-1.0]])],"derivedFrom":subQ0})])],"isStart":true});}
            var Q62;
            {var subQ0=sQuery(id+"F0.wireOp",EDGE,"E3");Q62=makeQuery(id+"F1.opExtrude","CAP_EDGE",EDGE,{"disambiguationData":[OSD([subQ0]),TDD([makeQuery(id+"F0.imprint","IMPRINT",EDGE,{"disambiguationData":[TD([[makeQuery(id+"F0.imprint","INTERSECT",VERTEX,{"derivedFrom":[sQuery(id+"F0.wireOp",EDGE,"E1"),subQ0]}),-1.0]])],"derivedFrom":subQ0})])],"isStart":true});}
            var Q63;
            {var subQ0=sQuery(id+"F0.wireOp",EDGE,"E2");Q63=makeQuery(id+"F1.opExtrude","CAP_EDGE",EDGE,{"disambiguationData":[OSD([subQ0]),TDD([makeQuery(id+"F0.imprint","IMPRINT",EDGE,{"disambiguationData":[TD([[makeQuery(id+"F0.imprint","INTERSECT",VERTEX,{"derivedFrom":[subQ0,sQuery(id+"F0.wireOp",EDGE,"E4")]}),1.0]])],"derivedFrom":subQ0})])],"isStart":true});}
            fillet(context, id + "F2", {"entities" : qUnion([Q0, Q1, Q2, Q3, Q4, Q5, Q6, Q7, Q8, Q9, Q10, Q11, Q12, Q13, Q14, Q15, Q16, Q17, Q18, Q19, Q20, Q21, Q22, Q23, Q24, Q25, Q26, Q27, Q28, Q29, Q30, Q31, Q32, Q33, Q34, Q35, Q36, Q37, Q38, Q39, Q40, Q41, Q42, Q43, Q44, Q45, Q46, Q47, Q48, Q49, Q50, Q51, Q52, Q53, Q54, Q55, Q56, Q57, Q58, Q59, Q60, Q61, Q62, Q63]), "radius" : 9.2 * mm, "tangentPropagation" : true, "allowEdgeOverflow" : false});
        }
        {
            var Q0;
            Q0=makeQuery(id+"F1.opExtrude","SWEPT_BODY",BODY,{"disambiguationData":[OSD([sQuery(id+"F0.wireOp",EDGE,"E0"),sQuery(id+"F0.wireOp",EDGE,"E1"),sQuery(id+"F0.wireOp",EDGE,"E5")])]});
            var Q1;
            Q1=makeQuery(id+"F1.opExtrude","SWEPT_BODY",BODY,{"disambiguationData":[OSD([sQuery(id+"F0.wireOp",EDGE,"E1"),sQuery(id+"F0.wireOp",EDGE,"E3"),sQuery(id+"F0.wireOp",EDGE,"E4"),sQuery(id+"F0.wireOp",EDGE,"E6"),sQuery(id+"F0.wireOp",EDGE,"E8.0"),sQuery(id+"F0.wireOp",EDGE,"E8.2")])]});
            var Q2;
            Q2=makeQuery(id+"F1.opExtrude","SWEPT_BODY",BODY,{"disambiguationData":[OSD([sQuery(id+"F0.wireOp",EDGE,"E1"),sQuery(id+"F0.wireOp",EDGE,"E2"),sQuery(id+"F0.wireOp",EDGE,"E3"),sQuery(id+"F0.wireOp",EDGE,"E4"),sQuery(id+"F0.wireOp",EDGE,"E6")])]});
            var Q3;
            Q3=makeQuery(id+"F1.opExtrude","SWEPT_BODY",BODY,{"disambiguationData":[OSD([sQuery(id+"F0.wireOp",EDGE,"E2"),sQuery(id+"F0.wireOp",EDGE,"E3"),sQuery(id+"F0.wireOp",EDGE,"E4"),sQuery(id+"F0.wireOp",EDGE,"E5"),sQuery(id+"F0.wireOp",EDGE,"E7")])]});
            var Q4;
            Q4=makeQuery(id+"F1.opExtrude","SWEPT_BODY",BODY,{"disambiguationData":[OSD([sQuery(id+"F0.wireOp",EDGE,"E2"),sQuery(id+"F0.wireOp",EDGE,"E3"),sQuery(id+"F0.wireOp",EDGE,"E4"),sQuery(id+"F0.wireOp",EDGE,"E6"),sQuery(id+"F0.wireOp",EDGE,"E7"),sQuery(id+"F0.wireOp",EDGE,"E8.1"),sQuery(id+"F0.wireOp",EDGE,"E8.2")])]});
            var Q5;
            Q5=makeQuery(id+"F1.opExtrude","SWEPT_BODY",BODY,{"disambiguationData":[OSD([sQuery(id+"F0.wireOp",EDGE,"E2"),sQuery(id+"F0.wireOp",EDGE,"E4"),sQuery(id+"F0.wireOp",EDGE,"E5"),sQuery(id+"F0.wireOp",EDGE,"E7"),sQuery(id+"F0.wireOp",EDGE,"E8.0"),sQuery(id+"F0.wireOp",EDGE,"E8.1")])]});
            var Q6;
            Q6=makeQuery(id+"F1.opExtrude","SWEPT_BODY",BODY,{"disambiguationData":[OSD([sQuery(id+"F0.wireOp",EDGE,"E2"),sQuery(id+"F0.wireOp",EDGE,"E3"),sQuery(id+"F0.wireOp",EDGE,"E4"),sQuery(id+"F0.wireOp",EDGE,"E7")])]});
            var Q7;
            Q7=makeQuery(id+"F1.opExtrude","SWEPT_FACE",FACE,{"disambiguationData":[OSD([sQuery(id+"F0.wireOp",EDGE,"E0")])]});
            mirror(context, id + "F3", {"operationType" : NewBodyOperationType.ADD, "entities" : qUnion([Q0, Q1, Q2, Q3, Q4, Q5, Q6]), "mirrorPlane" : qUnion([Q7])});
        }
        {
            var Q0;
            {var subQ0=sQuery(id+"F0.wireOp",EDGE,"E1");Q0=makeQuery(id+"F1.opExtrude","CAP_EDGE",EDGE,{"disambiguationData":[OSD([subQ0]),TDD([makeQuery(id+"F0.imprint","IMPRINT",EDGE,{"disambiguationData":[TD([[makeQuery(id+"F0.imprint","INTERSECT",VERTEX,{"derivedFrom":[sQuery(id+"F0.wireOp",EDGE,"E0"),subQ0]}),-1.0]])],"derivedFrom":subQ0})])],"isStart":true});}
            var Q1;
            {var subQ0=sQuery(id+"F0.wireOp",EDGE,"E1");Q1=makeQuery(id+"F3.opPattern","COPY",EDGE,{"derivedFrom":makeQuery(id+"F1.opExtrude","CAP_EDGE",EDGE,{"disambiguationData":[OSD([subQ0]),TDD([makeQuery(id+"F0.imprint","IMPRINT",EDGE,{"disambiguationData":[TD([[makeQuery(id+"F0.imprint","INTERSECT",VERTEX,{"derivedFrom":[sQuery(id+"F0.wireOp",EDGE,"E0"),subQ0]}),-1.0]])],"derivedFrom":subQ0})])],"isStart":true}),"instanceName":"1"});}
            var Q2;
            {var subQ0=sQuery(id+"F0.wireOp",EDGE,"E5");Q2=makeQuery(id+"F1.opExtrude","CAP_EDGE",EDGE,{"disambiguationData":[OSD([subQ0]),TDD([makeQuery(id+"F0.imprint","IMPRINT",EDGE,{"disambiguationData":[TD([[makeQuery(id+"F0.imprint","INTERSECT",VERTEX,{"derivedFrom":[sQuery(id+"F0.wireOp",EDGE,"E0"),subQ0]}),-1.0]])],"derivedFrom":subQ0})])],"isStart":true});}
            var Q3;
            {var subQ0=sQuery(id+"F0.wireOp",EDGE,"E5");Q3=makeQuery(id+"F3.opPattern","COPY",EDGE,{"derivedFrom":makeQuery(id+"F1.opExtrude","CAP_EDGE",EDGE,{"disambiguationData":[OSD([subQ0]),TDD([makeQuery(id+"F0.imprint","IMPRINT",EDGE,{"disambiguationData":[TD([[makeQuery(id+"F0.imprint","INTERSECT",VERTEX,{"derivedFrom":[sQuery(id+"F0.wireOp",EDGE,"E0"),subQ0]}),-1.0]])],"derivedFrom":subQ0})])],"isStart":true}),"instanceName":"1"});}
            var Q4;
            {var subQ0=sQuery(id+"F0.wireOp",EDGE,"E5");Q4=makeQuery(id+"F3.opPattern","COPY",EDGE,{"derivedFrom":makeQuery(id+"F1.opExtrude","CAP_EDGE",EDGE,{"disambiguationData":[OSD([subQ0]),TDD([makeQuery(id+"F0.imprint","IMPRINT",EDGE,{"disambiguationData":[TD([[makeQuery(id+"F0.imprint","INTERSECT",VERTEX,{"derivedFrom":[sQuery(id+"F0.wireOp",EDGE,"E0"),subQ0]}),-1.0]])],"derivedFrom":subQ0})])],"isStart":false}),"instanceName":"1"});}
            var Q5;
            {var subQ0=sQuery(id+"F0.wireOp",EDGE,"E5");Q5=makeQuery(id+"F1.opExtrude","CAP_EDGE",EDGE,{"disambiguationData":[OSD([subQ0]),TDD([makeQuery(id+"F0.imprint","IMPRINT",EDGE,{"disambiguationData":[TD([[makeQuery(id+"F0.imprint","INTERSECT",VERTEX,{"derivedFrom":[sQuery(id+"F0.wireOp",EDGE,"E0"),subQ0]}),-1.0]])],"derivedFrom":subQ0})])],"isStart":false});}
            var Q6;
            {var subQ0=sQuery(id+"F0.wireOp",EDGE,"E1");Q6=makeQuery(id+"F1.opExtrude","CAP_EDGE",EDGE,{"disambiguationData":[OSD([subQ0]),TDD([makeQuery(id+"F0.imprint","IMPRINT",EDGE,{"disambiguationData":[TD([[makeQuery(id+"F0.imprint","INTERSECT",VERTEX,{"derivedFrom":[sQuery(id+"F0.wireOp",EDGE,"E0"),subQ0]}),-1.0]])],"derivedFrom":subQ0})])],"isStart":false});}
            var Q7;
            {var subQ0=sQuery(id+"F0.wireOp",EDGE,"E1");Q7=makeQuery(id+"F3.opPattern","COPY",EDGE,{"derivedFrom":makeQuery(id+"F1.opExtrude","CAP_EDGE",EDGE,{"disambiguationData":[OSD([subQ0]),TDD([makeQuery(id+"F0.imprint","IMPRINT",EDGE,{"disambiguationData":[TD([[makeQuery(id+"F0.imprint","INTERSECT",VERTEX,{"derivedFrom":[sQuery(id+"F0.wireOp",EDGE,"E0"),subQ0]}),-1.0]])],"derivedFrom":subQ0})])],"isStart":false}),"instanceName":"1"});}
            fillet(context, id + "F4", {"entities" : qUnion([Q0, Q1, Q2, Q3, Q4, Q5, Q6, Q7]), "radius" : 9.2 * mm, "tangentPropagation" : true, "allowEdgeOverflow" : false});
        }
    });
